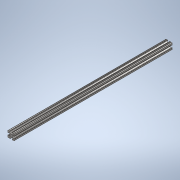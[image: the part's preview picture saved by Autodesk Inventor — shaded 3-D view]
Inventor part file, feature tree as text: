
AUTODESK INVENTOR PART (.ipt)
format: ipt  version: 2020 (Build 240168000, 168)  size: 242,688 bytes
history: native  units: in
note: dims shown in document units (in); Inventor stores cm internally (conversion verified against a paired STEP export)
features: extrude x1, sketch x1
ambient origin geometry x8: Origin, YZ Plane, XZ Plane, XY Plane, X Axis, Y Axis, Z Axis, Center Point
bodies: Solid1 (feature_tree)
feature tree (2):
  extrude  "Extrusion1"  [1 undecoded]
  sketch  "Sketch1"  dims[d0=24.0in d1=0.0in]
note: 1 required parameter value undecoded (feature->parameter linkage not recoverable at this tier; creation-order binding heuristic only, values carry confidence <= 0.55)
